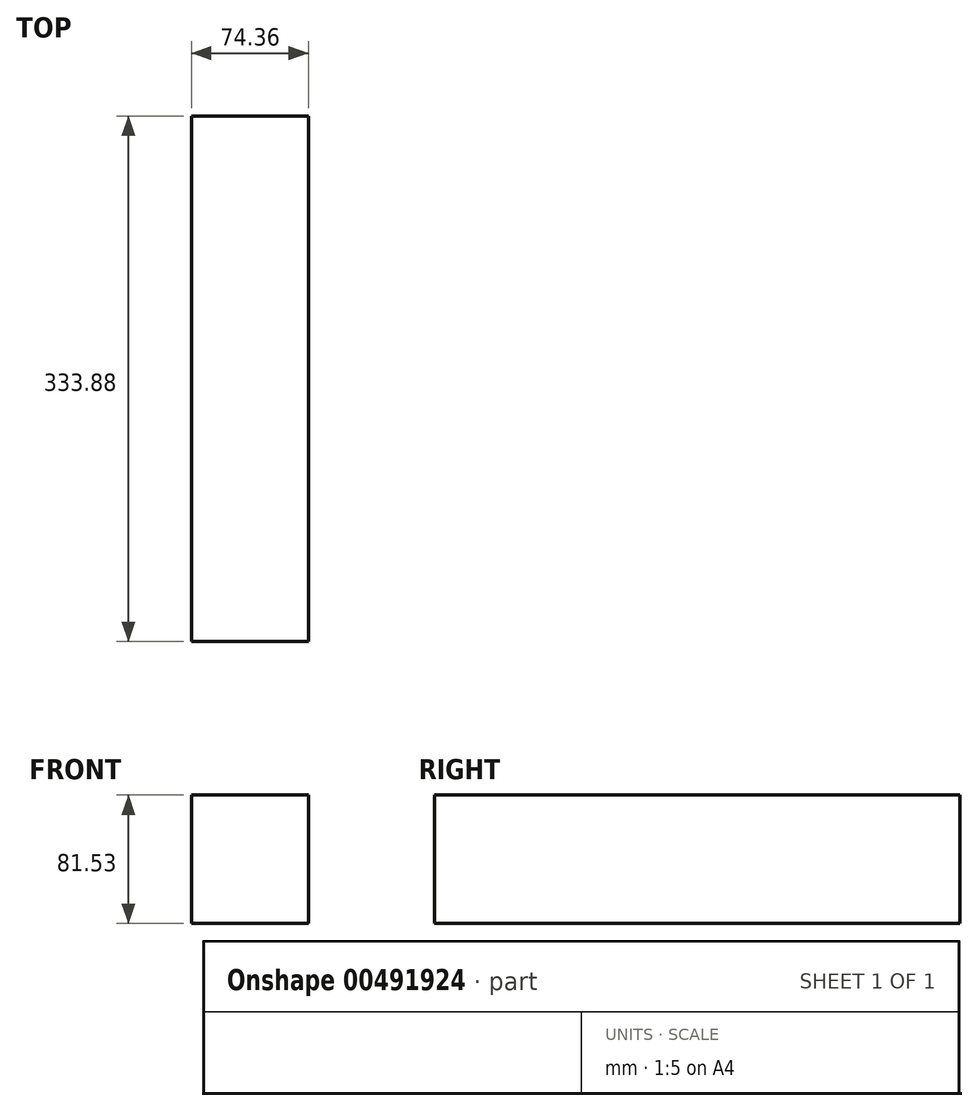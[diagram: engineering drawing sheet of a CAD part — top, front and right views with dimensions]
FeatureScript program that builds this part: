
annotation { "Feature Type Name" : "Feature", "Feature Type Description" : "" }
export const myFeature = defineFeature(function(context is Context, id is Id, definition is map)
    precondition{}
    {
        {
            var Q0;
            Q0=qCreatedBy(makeId("Top.planeOp"),FACE);
            var sketch = newSketch(context, id + "F0", { "sketchPlane" : qUnion([Q0])});
            skLineSegment(sketch, "E0.bottom", {"start": v(-37.18, 166.94) * mm, "end": v(37.18, 166.94) * mm});
            skLineSegment(sketch, "E0.top", {"start": v(-37.18, -166.94) * mm, "end": v(37.18, -166.94) * mm});
            skLineSegment(sketch, "E0.left", {"start": v(-37.18, 166.94) * mm, "end": v(-37.18, -166.94) * mm});
            skLineSegment(sketch, "E0.right", {"start": v(37.18, 166.94) * mm, "end": v(37.18, -166.94) * mm});
            skPoint(sketch, "E0.middle", {"position": v(0, 0) * mm});
            skSolve(sketch);
        }
        {
            var Q0;
            Q0=makeQuery(id+"F0.imprint","IMPRINT",FACE,{"disambiguationData":[TD([[makeQuery(id+"F0.imprint","IMPRINT",EDGE,{"derivedFrom":sQuery(id+"F0.wireOp",EDGE,"E0.bottom")}),-1.0]])]});
            extrude(context, id + "F1", {"entities" : qUnion([Q0]), "depth" : 81.53 * mm});
        }
    });
